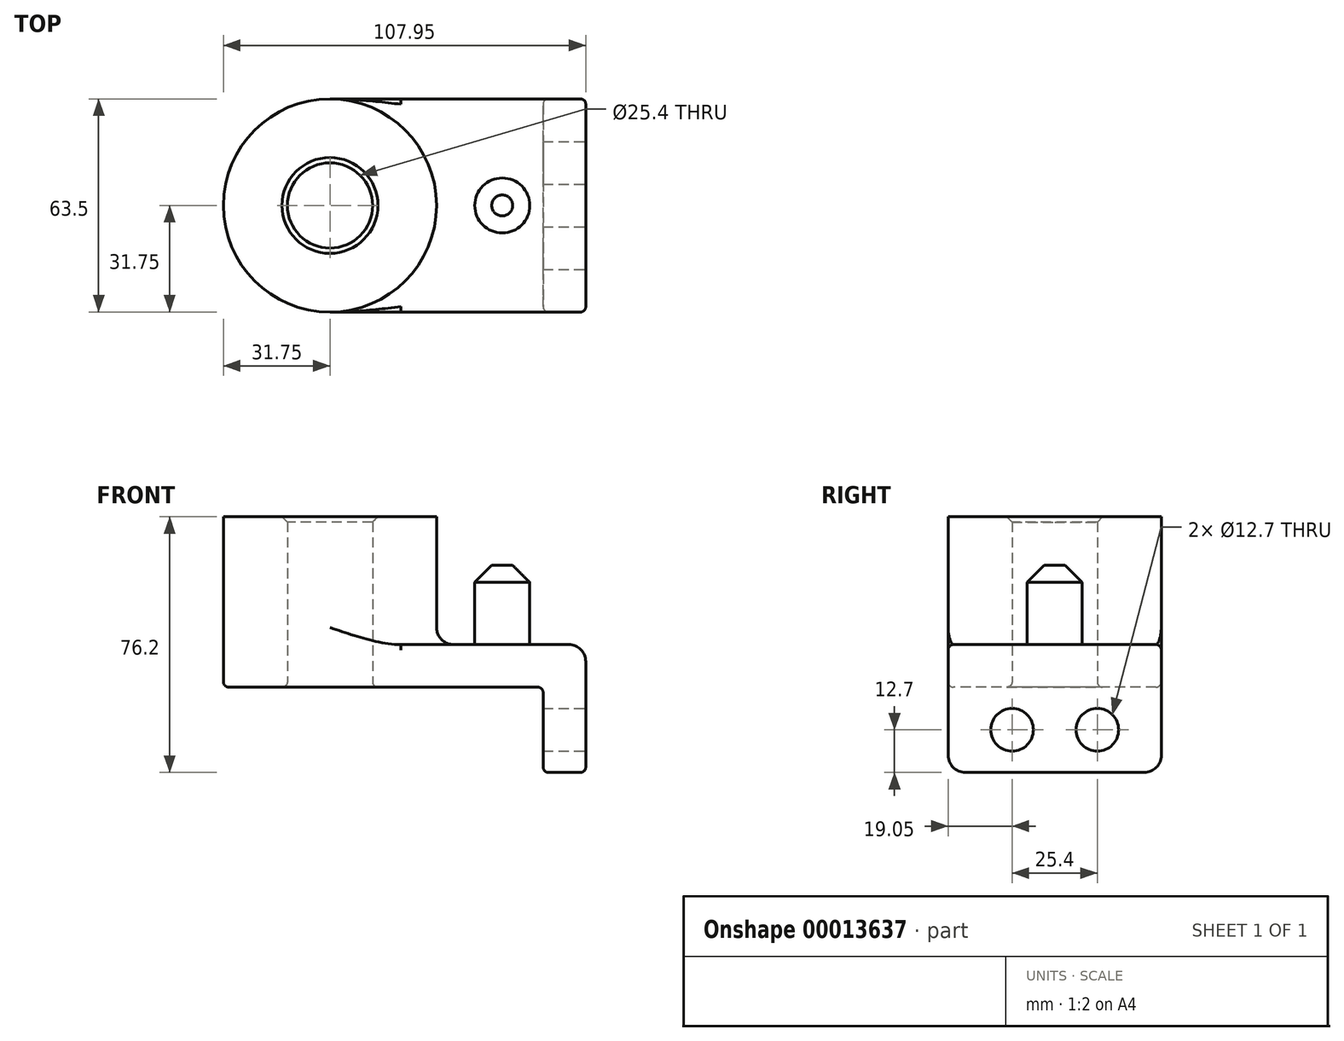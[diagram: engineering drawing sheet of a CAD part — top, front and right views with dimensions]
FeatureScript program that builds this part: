
annotation { "Feature Type Name" : "Feature", "Feature Type Description" : "" }
export const myFeature = defineFeature(function(context is Context, id is Id, definition is map)
    precondition{}
    {
        {
            var Q0;
            Q0=qCreatedBy(makeId("Top.planeOp"),FACE);
            var sketch = newSketch(context, id + "F0", { "sketchPlane" : qUnion([Q0])});
            skLineSegment(sketch, "E0.rect.bottom", {"start": v(38.1, 31.75) * mm, "end": v(-38.1, 31.75) * mm});
            skLineSegment(sketch, "E0.rect.top", {"start": v(38.1, -31.75) * mm, "end": v(-38.1, -31.75) * mm});
            skLineSegment(sketch, "E0.rect.left", {"start": v(38.1, 31.75) * mm, "end": v(38.1, -31.75) * mm});
            skLineSegment(sketch, "E0.rect.right", {"start": v(-38.1, 31.75) * mm, "end": v(-38.1, -31.75) * mm});
            skPoint(sketch, "E0.rect.middle", {"position": v(0, 0) * mm});
            skCircle(sketch, "E1", {"center": v(-38.1, 0) * mm, "radius": 31.75 * mm});
            skCircle(sketch, "E2", {"center": v(-38.1, 0) * mm, "radius": 12.7 * mm});
            skSolve(sketch);
        }
        {
            var Q0;
            {var subQ3=sQuery(id+"F0.wireOp",EDGE,"E0.rect.bottom");Q0=makeQuery(id+"F0.imprint","IMPRINT",FACE,{"disambiguationData":[TD([[makeQuery(id+"F0.imprint","IMPRINT",EDGE,{"derivedFrom":subQ3}),1.0]])]});}
            var Q1;
            {var subQ0=sQuery(id+"F0.wireOp",EDGE,"E2");var subQ1=sQuery(id+"F0.wireOp",EDGE,"E0.rect.right");var subQ3=makeQuery(id+"F0.imprint","INTERSECT",VERTEX,{"disambiguationData":[OD(0.0)],"derivedFrom":[subQ1,subQ0]});Q1=makeQuery(id+"F0.imprint","IMPRINT",FACE,{"disambiguationData":[TD([[makeQuery(id+"F0.imprint","IMPRINT",EDGE,{"disambiguationData":[TD([[subQ3,-1.0]])],"derivedFrom":subQ0}),-1.0]])]});}
            var Q2;
            {var subQ0=sQuery(id+"F0.wireOp",EDGE,"E2");var subQ1=sQuery(id+"F0.wireOp",EDGE,"E0.rect.right");var subQ3=makeQuery(id+"F0.imprint","INTERSECT",VERTEX,{"disambiguationData":[OD(0.0)],"derivedFrom":[subQ1,subQ0]});Q2=makeQuery(id+"F0.imprint","IMPRINT",FACE,{"disambiguationData":[TD([[makeQuery(id+"F0.imprint","IMPRINT",EDGE,{"disambiguationData":[TD([[subQ3,1.0]])],"derivedFrom":subQ0}),-1.0]])]});}
            extrude(context, id + "F1", {"entities" : qUnion([Q0, Q1, Q2]), "depth" : 12.7 * mm});
        }
        {
            var Q0;
            {var subQ0=sQuery(id+"F0.wireOp",EDGE,"E2");var subQ1=sQuery(id+"F0.wireOp",EDGE,"E0.rect.right");var subQ3=makeQuery(id+"F0.imprint","INTERSECT",VERTEX,{"disambiguationData":[OD(0.0)],"derivedFrom":[subQ1,subQ0]});Q0=makeQuery(id+"F0.imprint","IMPRINT",FACE,{"disambiguationData":[TD([[makeQuery(id+"F0.imprint","IMPRINT",EDGE,{"disambiguationData":[TD([[subQ3,1.0]])],"derivedFrom":subQ0}),-1.0]])]});}
            var Q1;
            {var subQ0=sQuery(id+"F0.wireOp",EDGE,"E2");var subQ1=sQuery(id+"F0.wireOp",EDGE,"E0.rect.right");var subQ3=makeQuery(id+"F0.imprint","INTERSECT",VERTEX,{"disambiguationData":[OD(0.0)],"derivedFrom":[subQ1,subQ0]});Q1=makeQuery(id+"F0.imprint","IMPRINT",FACE,{"disambiguationData":[TD([[makeQuery(id+"F0.imprint","IMPRINT",EDGE,{"disambiguationData":[TD([[subQ3,-1.0]])],"derivedFrom":subQ0}),-1.0]])]});}
            extrude(context, id + "F2", {"entities" : qUnion([Q0, Q1]), "operationType" : NewBodyOperationType.ADD, "depth" : 50.8 * mm});
        }
        {
            var Q0;
            Q0=makeQuery(id+"F1.opExtrude","SWEPT_FACE",FACE,{"disambiguationData":[OSD([sQuery(id+"F0.wireOp",EDGE,"E0.rect.left")])]});
            var sketch = newSketch(context, id + "F3", { "sketchPlane" : qUnion([Q0])});
            skLineSegment(sketch, "E3.bottom", {"start": v(-31.75, 12.7) * mm, "end": v(31.75, 12.7) * mm});
            skLineSegment(sketch, "E3.top", {"start": v(-31.75, -25.4) * mm, "end": v(31.75, -25.4) * mm});
            skLineSegment(sketch, "E3.left", {"start": v(-31.75, 12.7) * mm, "end": v(-31.75, -25.4) * mm});
            skLineSegment(sketch, "E3.right", {"start": v(31.75, 12.7) * mm, "end": v(31.75, -25.4) * mm});
            skCircle(sketch, "E4", {"center": v(-12.7, -12.7) * mm, "radius": 6.35 * mm});
            skLineSegment(sketch, "E5", {"start": v(0, 12.7) * mm, "end": v(0, -25.4) * mm, "construction": true});
            skCircle(sketch, "E6.MirrorC", {"center": v(12.7, -12.7) * mm, "radius": 6.35 * mm});
            skSolve(sketch);
        }
        {
            var Q0;
            {var subQ2=sQuery(id+"F3.wireOp",EDGE,"E3.top");Q0=makeQuery(id+"F3.imprint","IMPRINT",FACE,{"disambiguationData":[TD([[makeQuery(id+"F3.imprint","IMPRINT",EDGE,{"derivedFrom":subQ2}),1.0]])]});}
            extrude(context, id + "F4", {"entities" : qUnion([Q0]), "operationType" : NewBodyOperationType.ADD, "oppositeDirection" : true, "depth" : 12.7 * mm});
        }
        {
            var Q0;
            {var subQ0=sQuery(id+"F0.wireOp",EDGE,"E1");Q0=makeQuery(id+"F2.boolean.opBoolean","INTERSECT",EDGE,{"derivedFrom":[makeQuery(id+"F1.opExtrude","CAP_FACE",FACE,{"disambiguationData":[OSD([sQuery(id+"F0.wireOp",EDGE,"E0.rect.bottom"),sQuery(id+"F0.wireOp",EDGE,"E0.rect.top"),sQuery(id+"F0.wireOp",EDGE,"E0.rect.left"),subQ0,sQuery(id+"F0.wireOp",EDGE,"E2")])],"isStart":false}),makeQuery(id+"F2.opExtrude","SWEPT_FACE",FACE,{"disambiguationData":[OSD([subQ0])]})]});}
            var Q1;
            Q1=makeQuery(id+"F1.opExtrude","CAP_EDGE",EDGE,{"disambiguationData":[OSD([sQuery(id+"F0.wireOp",EDGE,"E0.rect.left")])],"isStart":false});
            var Q2;
            Q2=makeQuery(id+"F4.opExtrude","SWEPT_EDGE",EDGE,{"disambiguationData":[OSD([sQuery(id+"F3.wireOp",EDGE,"E3.top"),sQuery(id+"F3.wireOp",EDGE,"E3.left")])]});
            var Q3;
            Q3=makeQuery(id+"F4.opExtrude","SWEPT_EDGE",EDGE,{"disambiguationData":[OSD([sQuery(id+"F3.wireOp",EDGE,"E3.top"),sQuery(id+"F3.wireOp",EDGE,"E3.right")])]});
            fillet(context, id + "F5", {"entities" : qUnion([Q0, Q1, Q2, Q3]), "radius" : 5.08 * mm, "tangentPropagation" : true, "allowEdgeOverflow" : false});
        }
        {
            var Q0;
            Q0=makeQuery(id+"F1.opExtrude","CAP_EDGE",EDGE,{"disambiguationData":[OSD([sQuery(id+"F0.wireOp",EDGE,"E0.rect.top")])],"isStart":true});
            var Q1;
            Q1=makeQuery(id+"F4.opExtrude","CAP_EDGE",EDGE,{"disambiguationData":[OSD([sQuery(id+"F3.wireOp",EDGE,"E3.left")])],"isStart":false});
            var Q2;
            Q2=makeQuery(id+"F1.opExtrude","CAP_EDGE",EDGE,{"disambiguationData":[OSD([sQuery(id+"F0.wireOp",EDGE,"E0.rect.top")])],"isStart":false});
            var Q3;
            Q3=makeQuery(id+"F1.opExtrude","CAP_FACE",FACE,{"disambiguationData":[OSD([sQuery(id+"F0.wireOp",EDGE,"E0.rect.bottom"),sQuery(id+"F0.wireOp",EDGE,"E0.rect.top"),sQuery(id+"F0.wireOp",EDGE,"E0.rect.left"),sQuery(id+"F0.wireOp",EDGE,"E1"),sQuery(id+"F0.wireOp",EDGE,"E2")])],"isStart":true});
            fillet(context, id + "F6", {"entities" : qUnion([Q0, Q1, Q2, Q3]), "radius" : 1.59 * mm, "tangentPropagation" : true, "allowEdgeOverflow" : false});
        }
        {
            var Q0;
            {var subQ0=sQuery(id+"F0.wireOp",EDGE,"E2");Q0=makeQuery(id+"F2.boolean.opBoolean","MERGE",FACE,{"derivedFrom":[makeQuery(id+"F1.opExtrude","SWEPT_FACE",FACE,{"disambiguationData":[OSD([subQ0])]}),makeQuery(id+"F2.opExtrude","SWEPT_FACE",FACE,{"disambiguationData":[OSD([subQ0])]})]});}
            chamfer(context, id + "F7", {"entities" : qUnion([Q0]), "width" : 1.59 * mm, "tangentPropagation" : true});
        }
        {
            var Q0;
            Q0=makeQuery(id+"F1.opExtrude","CAP_FACE",FACE,{"disambiguationData":[OSD([sQuery(id+"F0.wireOp",EDGE,"E0.rect.bottom"),sQuery(id+"F0.wireOp",EDGE,"E0.rect.top"),sQuery(id+"F0.wireOp",EDGE,"E0.rect.left"),sQuery(id+"F0.wireOp",EDGE,"E1"),sQuery(id+"F0.wireOp",EDGE,"E2")])],"isStart":false});
            var sketch = newSketch(context, id + "F8", { "sketchPlane" : qUnion([Q0])});
            skCircle(sketch, "E7", {"center": v(13.23, 0) * mm, "radius": 8.2 * mm});
            skSolve(sketch);
        }
        {
            var Q0;
            Q0=makeQuery(id+"F8.imprint","IMPRINT",FACE,{"disambiguationData":[TD([[makeQuery(id+"F8.imprint","IMPRINT",EDGE,{"derivedFrom":sQuery(id+"F8.wireOp",EDGE,"E7")}),1.0]])]});
            extrude(context, id + "F9", {"entities" : qUnion([Q0]), "operationType" : NewBodyOperationType.ADD, "depth" : 23.62 * mm});
        }
        {
            var Q0;
            Q0=makeQuery(id+"F9.opExtrude","CAP_EDGE",EDGE,{"disambiguationData":[OSD([sQuery(id+"F8.wireOp",EDGE,"E7")])],"isStart":false});
            chamfer(context, id + "F10", {"entities" : qUnion([Q0]), "width" : 5.08 * mm, "tangentPropagation" : true});
        }
    });
